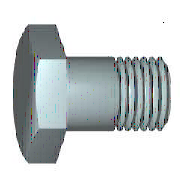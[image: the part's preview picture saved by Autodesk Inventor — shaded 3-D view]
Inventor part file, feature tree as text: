
AUTODESK INVENTOR PART (.ipt)
format: ipt  version: 2020 (Build 240168000, 168)  size: 200,192 bytes
history: native  units: mm (DEFAULTED — no unit token found)
features: sketch x4, other x4, plane x3, chamfer x1, fillet x1
ambient origin geometry x6: Origin, XY Plane, X Axis, Y Axis, Z Axis, Center Point
bodies: Solid1 (feature_tree)
feature tree (13):
  plane  "WorkPlane1"
  sketch  "Sketch1"  dims[d0=30.0mm]
  other  "WorkPoint1"
  chamfer  "Chamfer1"  Distance=5.3mm
  fillet  "Fillet1"  [1 undecoded]
  other  "MSC_A1"
  other  "MSC_PF1"
  other  "MSC_PT1"
  plane  "WorkPlane2"
  plane  "WorkPlane3"
  sketch  "Sketch2"  dims[d1=13.0mm]
  sketch  "Sketch3"  dims[d2=15.0mm]
  sketch  "Sketch4"  dims[d4=17.321016mm d6=5.3mm d7=0.0mm d8=15.0mm d10=0.0mm d12=30.0deg d14=360.0deg d15=0.0mm d17=10.0mm d18=4.0mm d19=80.0mm d20=40.0mm d21=360.0deg d22=0.625mm d23=0.625mm d24=0.4mm d25=0.1mm d26=0.0mm d27=60.0deg d28=6.5mm d29=0.0mm d30=0.0mm d32=0.0mm d33=0.0mm d34=0.0mm d37=0.0mm d38=0.0mm d39=45.0deg d40=0.0mm d41=0.0mm d42=0.0mm]
note: 1 required parameter value undecoded (feature->parameter linkage not recoverable at this tier; creation-order binding heuristic only, values carry confidence <= 0.55)
